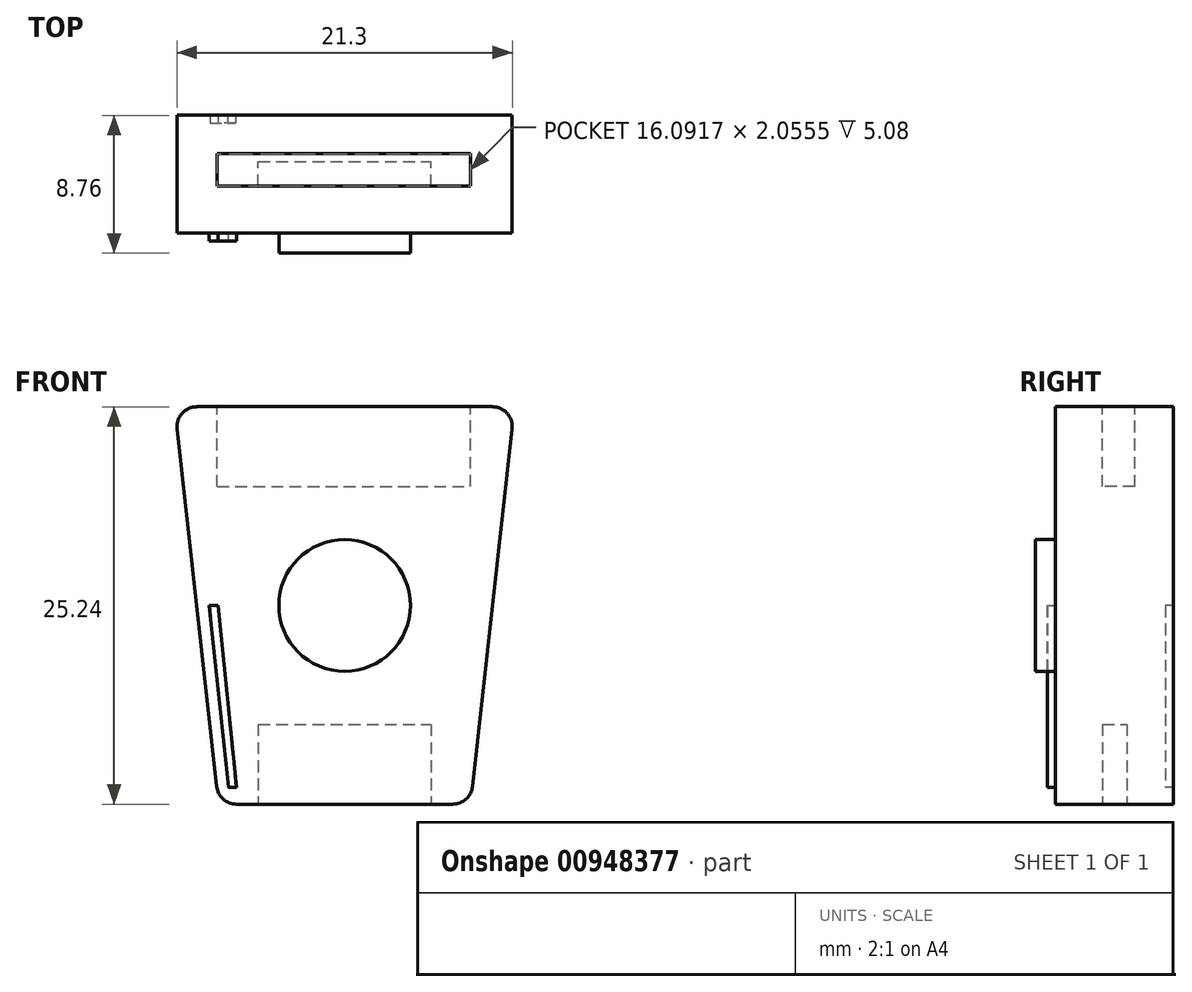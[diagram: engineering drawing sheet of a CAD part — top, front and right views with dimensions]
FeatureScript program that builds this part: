
annotation { "Feature Type Name" : "Feature", "Feature Type Description" : "" }
export const myFeature = defineFeature(function(context is Context, id is Id, definition is map)
    precondition{}
    {
        {
            var Q0;
            Q0=qCreatedBy(makeId("Front.planeOp"),FACE);
            var sketch = newSketch(context, id + "F0", { "sketchPlane" : qUnion([Q0])});
            skLineSegment(sketch, "E0", {"start": v(-10.8, 12.62) * mm, "end": v(10.8, 12.62) * mm});
            skLineSegment(sketch, "E1", {"start": v(10.8, 12.62) * mm, "end": v(8, -12.62) * mm});
            skLineSegment(sketch, "E2", {"start": v(8, -12.62) * mm, "end": v(-8, -12.62) * mm});
            skLineSegment(sketch, "E3", {"start": v(-8, -12.62) * mm, "end": v(-10.8, 12.62) * mm});
            skSolve(sketch);
        }
        {
            var Q0;
            Q0 = qSketchRegion(id + "F0", true);
            extrude(context, id + "F1", {"entities" : qUnion([Q0]), "oppositeDirection" : true, "depth" : 7 * mm, "offsetDistance" : 25.4 * mm});
        }
        {
            var Q0;
            Q0=makeQuery(id+"F1.opExtrude","CAP_FACE",FACE,{"disambiguationData":[OSD([sQuery(id+"F0.wireOp",EDGE,"E0"),sQuery(id+"F0.wireOp",EDGE,"E1"),sQuery(id+"F0.wireOp",EDGE,"E2"),sQuery(id+"F0.wireOp",EDGE,"E3")])],"isStart":true});
            var sketch = newSketch(context, id + "F2", { "sketchPlane" : qUnion([Q0])});
            skCircle(sketch, "E4", {"center": v(0, 0) * mm, "radius": 4.18 * mm});
            skSolve(sketch);
        }
        {
            var Q0;
            Q0=makeQuery(id+"F2.imprint","IMPRINT",FACE,{"disambiguationData":[TD([[makeQuery(id+"F2.imprint","IMPRINT",EDGE,{"derivedFrom":sQuery(id+"F2.wireOp",EDGE,"E4")}),1.0]])]});
            var Q1;
            Q1 = qSketchRegion(id + "F5", true);
            extrude(context, id + "F3", {"entities" : qUnion([Q0, Q1]), "operationType" : NewBodyOperationType.ADD, "depth" : 1.27 * mm, "offsetDistance" : 25.4 * mm});
        }
        {
            var Q0;
            Q0=makeQuery(id+"F1.opExtrude","CAP_FACE",FACE,{"disambiguationData":[OSD([sQuery(id+"F0.wireOp",EDGE,"E0"),sQuery(id+"F0.wireOp",EDGE,"E1"),sQuery(id+"F0.wireOp",EDGE,"E2"),sQuery(id+"F0.wireOp",EDGE,"E3")])],"isStart":true});
            var sketch = newSketch(context, id + "F4", { "sketchPlane" : qUnion([Q0])});
            skSolve(sketch);
        }
        {
            var Q0;
            Q0=makeQuery(id+"F4.imprint","IMPRINT",FACE,{"disambiguationData":[TD([[makeQuery(id+"F4.imprint","IMPRINT",EDGE,{"derivedFrom":makeQuery(id+"F1.opExtrude","CAP_EDGE",EDGE,{"disambiguationData":[OSD([sQuery(id+"F0.wireOp",EDGE,"E0")])],"isStart":true})}),-1.0]])]});
            var sketch = newSketch(context, id + "F5", { "sketchPlane" : qUnion([Q0])});
            skLineSegment(sketch, "E5", {"start": v(-8.6, 0) * mm, "end": v(-7.37, -11.55) * mm});
            skLineSegment(sketch, "E6", {"start": v(-6.86, -11.55) * mm, "end": v(-7.37, -11.55) * mm});
            skLineSegment(sketch, "E7", {"start": v(-8.6, 0) * mm, "end": v(-8.03, 0) * mm});
            skLineSegment(sketch, "E8", {"start": v(-6.86, -11.55) * mm, "end": v(-8.03, 0) * mm});
            skSolve(sketch);
        }
        {
            var Q0;
            Q0=makeQuery(id+"F5.imprint","IMPRINT",FACE,{"disambiguationData":[TD([[makeQuery(id+"F5.imprint","IMPRINT",EDGE,{"derivedFrom":sQuery(id+"F5.wireOp",EDGE,"E5")}),1.0]])]});
            var Q1;
            Q1=makeQuery(id+"F1.opExtrude","CAP_FACE",FACE,{"disambiguationData":[OSD([sQuery(id+"F0.wireOp",EDGE,"E0"),sQuery(id+"F0.wireOp",EDGE,"E1"),sQuery(id+"F0.wireOp",EDGE,"E2"),sQuery(id+"F0.wireOp",EDGE,"E3")])],"isStart":false});
            extrude(context, id + "F6", {"entities" : qUnion([Q0, Q1]), "operationType" : NewBodyOperationType.ADD, "depth" : 0.5 * mm, "offsetDistance" : 25.4 * mm});
        }
        {
            var Q0;
            Q0=makeQuery(id+"F1.opExtrude","CAP_FACE",FACE,{"disambiguationData":[OSD([sQuery(id+"F0.wireOp",EDGE,"E0"),sQuery(id+"F0.wireOp",EDGE,"E1"),sQuery(id+"F0.wireOp",EDGE,"E2"),sQuery(id+"F0.wireOp",EDGE,"E3")])],"isStart":false});
            var sketch = newSketch(context, id + "F7", { "sketchPlane" : qUnion([Q0])});
            skLineSegment(sketch, "E9", {"start": v(8.56, 0) * mm, "end": v(7.42, -11.55) * mm});
            skLineSegment(sketch, "E10", {"start": v(8.56, 0) * mm, "end": v(8.05, 0) * mm});
            skLineSegment(sketch, "E11", {"start": v(7.42, -11.55) * mm, "end": v(6.91, -11.55) * mm});
            skLineSegment(sketch, "E12", {"start": v(6.91, -11.55) * mm, "end": v(8.05, 0) * mm});
            skSolve(sketch);
        }
        {
            var Q0;
            Q0=makeQuery(id+"F7.imprint","IMPRINT",FACE,{"disambiguationData":[TD([[makeQuery(id+"F7.imprint","IMPRINT",EDGE,{"derivedFrom":sQuery(id+"F7.wireOp",EDGE,"E9")}),1.0]])]});
            extrude(context, id + "F8", {"entities" : qUnion([Q0]), "operationType" : NewBodyOperationType.ADD, "depth" : 0.5 * mm, "offsetDistance" : 25.4 * mm});
        }
        {
            var Q0;
            Q0=makeQuery(id+"F1.opExtrude","SWEPT_EDGE",EDGE,{"disambiguationData":[OSD([sQuery(id+"F0.wireOp",EDGE,"E0"),sQuery(id+"F0.wireOp",EDGE,"E3")])]});
            var Q1;
            Q1=makeQuery(id+"F1.opExtrude","SWEPT_EDGE",EDGE,{"disambiguationData":[OSD([sQuery(id+"F0.wireOp",EDGE,"E0"),sQuery(id+"F0.wireOp",EDGE,"E1")])]});
            var Q2;
            Q2=makeQuery(id+"F1.opExtrude","SWEPT_EDGE",EDGE,{"disambiguationData":[OSD([sQuery(id+"F0.wireOp",EDGE,"E1"),sQuery(id+"F0.wireOp",EDGE,"E2")])]});
            var Q3;
            Q3=makeQuery(id+"F1.opExtrude","SWEPT_EDGE",EDGE,{"disambiguationData":[OSD([sQuery(id+"F0.wireOp",EDGE,"E2"),sQuery(id+"F0.wireOp",EDGE,"E3")])]});
            fillet(context, id + "F9", {"entities" : qUnion([Q0, Q1, Q2, Q3]), "radius" : 1.27 * mm, "tangentPropagation" : true, "allowEdgeOverflow" : false});
        }
        {
            var Q0;
            {var subQ0=sQuery(id+"F0.wireOp",EDGE,"E0");Q0=makeQuery(id+"F8.boolean.opBoolean","MERGE",FACE,{"derivedFrom":[makeQuery(id+"F1.opExtrude","SWEPT_FACE",FACE,{"disambiguationData":[OSD([subQ0])]}),makeQuery(id+"F8.opExtrude","SWEPT_FACE",FACE,{"disambiguationData":[OSD([subQ0])]})]});}
            var sketch = newSketch(context, id + "F10", { "sketchPlane" : qUnion([Q0])});
            skLineSegment(sketch, "E13.bottom", {"start": v(-8.1, 5.05) * mm, "end": v(7.99, 5.05) * mm});
            skLineSegment(sketch, "E13.top", {"start": v(-8.1, 3) * mm, "end": v(7.99, 3) * mm});
            skLineSegment(sketch, "E13.left", {"start": v(-8.1, 5.05) * mm, "end": v(-8.1, 3) * mm});
            skLineSegment(sketch, "E13.right", {"start": v(7.99, 5.05) * mm, "end": v(7.99, 3) * mm});
            skSolve(sketch);
        }
        {
            var Q0;
            Q0=makeQuery(id+"F10.imprint","IMPRINT",FACE,{"disambiguationData":[TD([[makeQuery(id+"F10.imprint","IMPRINT",EDGE,{"derivedFrom":sQuery(id+"F10.wireOp",EDGE,"E13.bottom")}),-1.0]])]});
            var Q1;
            {var subQ0=sQuery(id+"F0.wireOp",EDGE,"E2");Q1=makeQuery(id+"F8.boolean.opBoolean","MERGE",FACE,{"derivedFrom":[makeQuery(id+"F1.opExtrude","SWEPT_FACE",FACE,{"disambiguationData":[OSD([subQ0])]}),makeQuery(id+"F8.opExtrude","SWEPT_FACE",FACE,{"disambiguationData":[OSD([subQ0])]})]});}
            extrude(context, id + "F11", {"entities" : qUnion([Q0, Q1]), "operationType" : NewBodyOperationType.REMOVE, "oppositeDirection" : true, "depth" : 5.08 * mm, "offsetDistance" : 25.4 * mm});
        }
        {
            var Q0;
            {var subQ0=sQuery(id+"F0.wireOp",EDGE,"E2");Q0=makeQuery(id+"F8.boolean.opBoolean","MERGE",FACE,{"derivedFrom":[makeQuery(id+"F1.opExtrude","SWEPT_FACE",FACE,{"disambiguationData":[OSD([subQ0])]}),makeQuery(id+"F8.opExtrude","SWEPT_FACE",FACE,{"disambiguationData":[OSD([subQ0])]})]});}
            var sketch = newSketch(context, id + "F12", { "sketchPlane" : qUnion([Q0])});
            skLineSegment(sketch, "E14.bottom", {"start": v(-5.5, -3) * mm, "end": v(5.47, -3) * mm});
            skLineSegment(sketch, "E14.top", {"start": v(-5.5, -4.56) * mm, "end": v(5.47, -4.56) * mm});
            skLineSegment(sketch, "E14.left", {"start": v(-5.5, -3) * mm, "end": v(-5.5, -4.56) * mm});
            skLineSegment(sketch, "E14.right", {"start": v(5.47, -3) * mm, "end": v(5.47, -4.56) * mm});
            skSolve(sketch);
        }
        {
            var Q0;
            Q0=makeQuery(id+"F12.imprint","IMPRINT",FACE,{"disambiguationData":[TD([[makeQuery(id+"F12.imprint","IMPRINT",EDGE,{"derivedFrom":sQuery(id+"F12.wireOp",EDGE,"E14.bottom")}),-1.0]])]});
            extrude(context, id + "F13", {"entities" : qUnion([Q0]), "operationType" : NewBodyOperationType.REMOVE, "oppositeDirection" : true, "depth" : 5.08 * mm, "offsetDistance" : 25.4 * mm});
        }
    });
